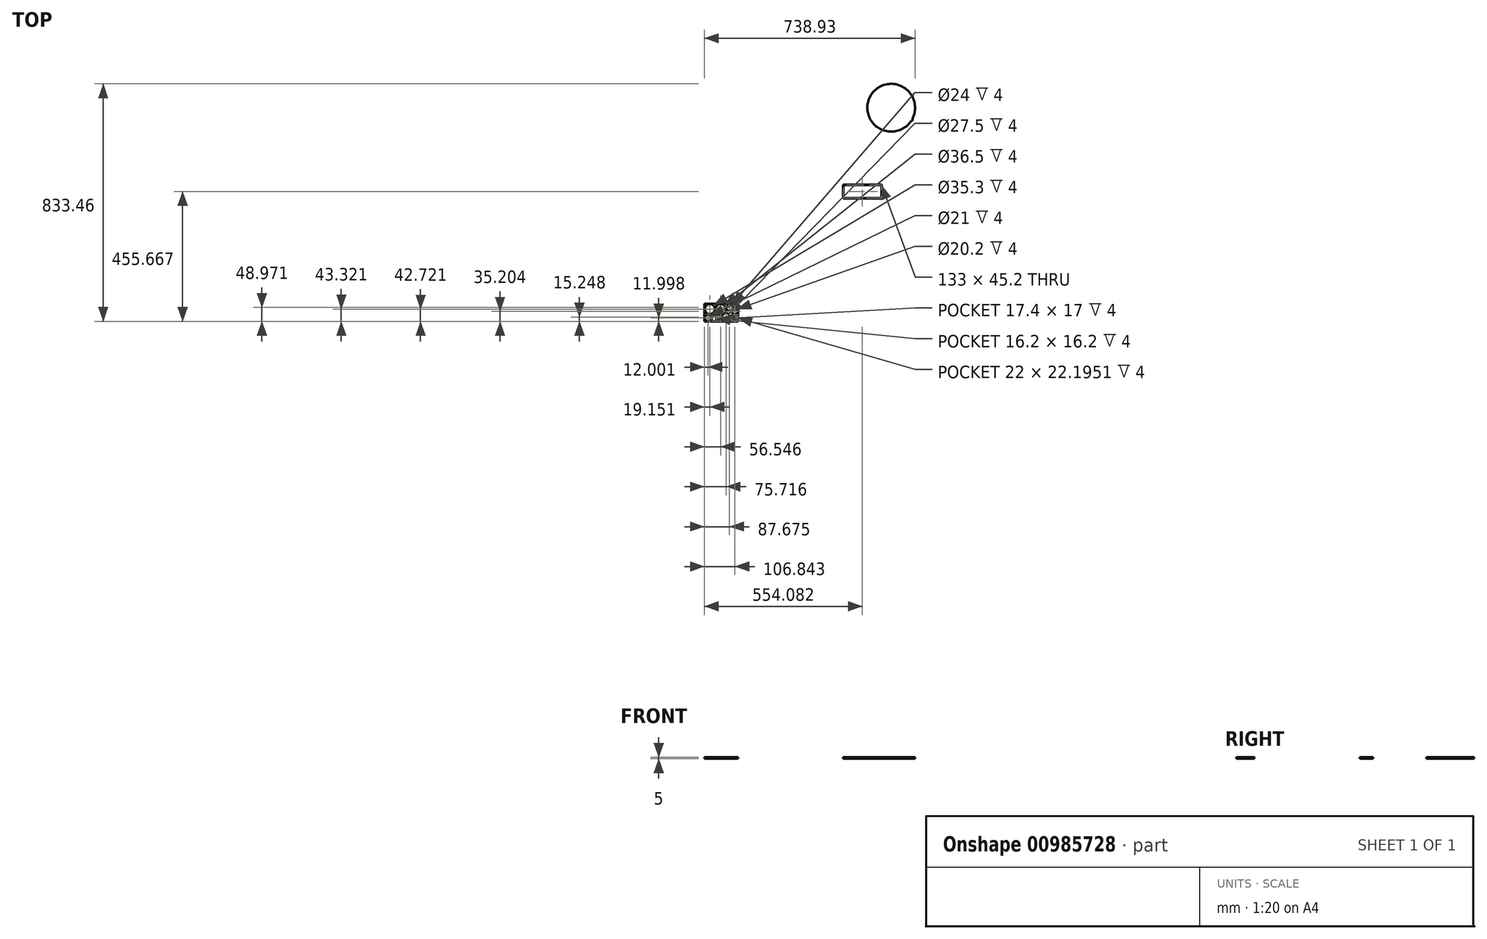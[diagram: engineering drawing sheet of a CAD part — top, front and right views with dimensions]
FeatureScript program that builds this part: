
annotation { "Feature Type Name" : "Feature", "Feature Type Description" : "" }
export const myFeature = defineFeature(function(context is Context, id is Id, definition is map)
    precondition{}
    {
        {
            var Q0;
            Q0=qCreatedBy(makeId("Top.planeOp"),FACE);
            var sketch = newSketch(context, id + "F0", { "sketchPlane" : qUnion([Q0])});
            skCircle(sketch, "E0", {"center": v(-761.21, 497.2) * mm, "radius": 83.82 * mm});
            skLineSegment(sketch, "E1.bottom", {"start": v(-832.69, 451.54) * mm, "end": v(-686.64, 451.54) * mm});
            skLineSegment(sketch, "E1.top", {"start": v(-832.69, 540.44) * mm, "end": v(-686.64, 540.44) * mm});
            skLineSegment(sketch, "E1.left", {"start": v(-832.69, 451.54) * mm, "end": v(-832.69, 540.44) * mm});
            skLineSegment(sketch, "E1.right", {"start": v(-686.64, 451.54) * mm, "end": v(-686.64, 540.44) * mm});
            skCircle(sketch, "E2.5.0.0", {"center": v(-1328.65, -203.47) * mm, "radius": 12 * mm});
            skCircle(sketch, "E3", {"center": v(-1340.6, -237.2) * mm, "radius": 13.75 * mm});
            skCircle(sketch, "E4", {"center": v(-1359.77, -209.72) * mm, "radius": 18.25 * mm});
            skCircle(sketch, "E5", {"center": v(-1397.17, -209.12) * mm, "radius": 17.65 * mm});
            skCircle(sketch, "E6", {"center": v(-1404.32, -240.44) * mm, "radius": 10.5 * mm});
            skCircle(sketch, "E7", {"center": v(-1309.48, -217.24) * mm, "radius": 10.1 * mm});
            skLineSegment(sketch, "E8.bottom", {"start": v(-1373.67, -250.94) * mm, "end": v(-1356.27, -250.94) * mm});
            skLineSegment(sketch, "E8.top", {"start": v(-1373.67, -233.94) * mm, "end": v(-1356.27, -233.94) * mm});
            skLineSegment(sketch, "E8.left", {"start": v(-1373.67, -250.94) * mm, "end": v(-1373.67, -233.94) * mm});
            skLineSegment(sketch, "E8.right", {"start": v(-1356.27, -250.94) * mm, "end": v(-1356.27, -233.94) * mm});
            skLineSegment(sketch, "E9.bottom", {"start": v(-1391.37, -250.94) * mm, "end": v(-1375.17, -250.94) * mm});
            skLineSegment(sketch, "E9.top", {"start": v(-1391.37, -234.74) * mm, "end": v(-1375.17, -234.74) * mm});
            skLineSegment(sketch, "E9.left", {"start": v(-1391.37, -250.94) * mm, "end": v(-1391.37, -234.74) * mm});
            skLineSegment(sketch, "E9.right", {"start": v(-1375.17, -250.94) * mm, "end": v(-1375.17, -234.74) * mm});
            skLineSegment(sketch, "E10.0.1.0", {"start": v(-1321.38, -250.94) * mm, "end": v(-1321.38, -228.94) * mm});
            skLineSegment(sketch, "E10.0.1.1", {"start": v(-1321.38, -228.94) * mm, "end": v(-1299.38, -228.75) * mm});
            skLineSegment(sketch, "E10.0.1.2", {"start": v(-1299.38, -250.94) * mm, "end": v(-1299.38, -228.75) * mm});
            skLineSegment(sketch, "E10.0.1.3", {"start": v(-1321.38, -250.94) * mm, "end": v(-1299.38, -250.94) * mm});
            skLineSegment(sketch, "E11.bottom", {"start": v(-1416.32, -252.44) * mm, "end": v(-1297.88, -252.44) * mm});
            skLineSegment(sketch, "E11.top", {"start": v(-1416.32, -189.97) * mm, "end": v(-1297.88, -189.97) * mm});
            skLineSegment(sketch, "E11.left", {"start": v(-1416.32, -252.44) * mm, "end": v(-1416.32, -189.97) * mm});
            skLineSegment(sketch, "E11.right", {"start": v(-1297.88, -252.44) * mm, "end": v(-1297.88, -189.97) * mm});
            skLineSegment(sketch, "E12.bottom", {"start": v(-929.94, 179.43) * mm, "end": v(-794.54, 179.43) * mm});
            skLineSegment(sketch, "E12.top", {"start": v(-929.94, 227.03) * mm, "end": v(-794.54, 227.03) * mm});
            skLineSegment(sketch, "E12.left", {"start": v(-929.94, 179.43) * mm, "end": v(-929.94, 227.03) * mm});
            skLineSegment(sketch, "E12.right", {"start": v(-794.54, 179.43) * mm, "end": v(-794.54, 227.03) * mm});
            skLineSegment(sketch, "E13.bottom", {"start": v(-928.74, 180.63) * mm, "end": v(-906.74, 180.63) * mm});
            skLineSegment(sketch, "E13.top", {"start": v(-928.74, 202.63) * mm, "end": v(-906.74, 202.63) * mm});
            skLineSegment(sketch, "E13.left", {"start": v(-928.74, 180.63) * mm, "end": v(-928.74, 202.63) * mm});
            skLineSegment(sketch, "E13.right", {"start": v(-906.74, 180.63) * mm, "end": v(-906.74, 202.63) * mm});
            skLineSegment(sketch, "E14.0.1.0", {"start": v(-928.74, 225.83) * mm, "end": v(-906.74, 225.83) * mm});
            skLineSegment(sketch, "E14.0.1.1", {"start": v(-928.74, 203.83) * mm, "end": v(-928.74, 225.83) * mm});
            skLineSegment(sketch, "E14.0.1.2", {"start": v(-906.74, 203.83) * mm, "end": v(-906.74, 225.83) * mm});
            skLineSegment(sketch, "E14.0.1.3", {"start": v(-928.74, 203.83) * mm, "end": v(-906.74, 203.83) * mm});
            skLineSegment(sketch, "E14.1.0.0", {"start": v(-906.74, 202.63) * mm, "end": v(-884.74, 202.63) * mm});
            skLineSegment(sketch, "E14.1.0.2", {"start": v(-884.74, 180.63) * mm, "end": v(-884.74, 202.63) * mm});
            skLineSegment(sketch, "E14.1.0.3", {"start": v(-906.74, 180.63) * mm, "end": v(-884.74, 180.63) * mm});
            skLineSegment(sketch, "E14.1.1.0", {"start": v(-906.74, 225.83) * mm, "end": v(-884.74, 225.83) * mm});
            skLineSegment(sketch, "E14.1.1.1", {"start": v(-906.74, 203.83) * mm, "end": v(-906.74, 225.83) * mm});
            skLineSegment(sketch, "E14.1.1.2", {"start": v(-884.74, 203.83) * mm, "end": v(-884.74, 225.83) * mm});
            skLineSegment(sketch, "E14.1.1.3", {"start": v(-906.74, 203.83) * mm, "end": v(-884.74, 203.83) * mm});
            skLineSegment(sketch, "E14.2.0.0", {"start": v(-884.74, 202.63) * mm, "end": v(-862.74, 202.63) * mm});
            skLineSegment(sketch, "E14.2.0.1", {"start": v(-884.74, 180.63) * mm, "end": v(-884.74, 202.63) * mm});
            skLineSegment(sketch, "E14.2.0.2", {"start": v(-862.74, 180.63) * mm, "end": v(-862.74, 202.63) * mm});
            skLineSegment(sketch, "E14.2.0.3", {"start": v(-884.74, 180.63) * mm, "end": v(-862.74, 180.63) * mm});
            skLineSegment(sketch, "E14.2.1.0", {"start": v(-884.74, 225.83) * mm, "end": v(-862.74, 225.83) * mm});
            skLineSegment(sketch, "E14.2.1.1", {"start": v(-884.74, 203.83) * mm, "end": v(-884.74, 225.83) * mm});
            skLineSegment(sketch, "E14.2.1.2", {"start": v(-862.74, 203.83) * mm, "end": v(-862.74, 225.83) * mm});
            skLineSegment(sketch, "E14.2.1.3", {"start": v(-884.74, 203.83) * mm, "end": v(-862.74, 203.83) * mm});
            skLineSegment(sketch, "E14.3.0.0", {"start": v(-862.74, 202.63) * mm, "end": v(-840.74, 202.63) * mm});
            skLineSegment(sketch, "E14.3.0.1", {"start": v(-862.74, 180.63) * mm, "end": v(-862.74, 202.63) * mm});
            skLineSegment(sketch, "E14.3.0.2", {"start": v(-840.74, 180.63) * mm, "end": v(-840.74, 202.63) * mm});
            skLineSegment(sketch, "E14.3.0.3", {"start": v(-862.74, 180.63) * mm, "end": v(-840.74, 180.63) * mm});
            skLineSegment(sketch, "E14.3.1.0", {"start": v(-862.74, 225.83) * mm, "end": v(-840.74, 225.83) * mm});
            skLineSegment(sketch, "E14.3.1.1", {"start": v(-862.74, 203.83) * mm, "end": v(-862.74, 225.83) * mm});
            skLineSegment(sketch, "E14.3.1.2", {"start": v(-840.74, 203.83) * mm, "end": v(-840.74, 225.83) * mm});
            skLineSegment(sketch, "E14.3.1.3", {"start": v(-862.74, 203.83) * mm, "end": v(-840.74, 203.83) * mm});
            skLineSegment(sketch, "E14.4.0.0", {"start": v(-840.74, 202.63) * mm, "end": v(-818.74, 202.63) * mm});
            skLineSegment(sketch, "E14.4.0.1", {"start": v(-840.74, 180.63) * mm, "end": v(-840.74, 202.63) * mm});
            skLineSegment(sketch, "E14.4.0.2", {"start": v(-818.74, 180.63) * mm, "end": v(-818.74, 202.63) * mm});
            skLineSegment(sketch, "E14.4.0.3", {"start": v(-840.74, 180.63) * mm, "end": v(-818.74, 180.63) * mm});
            skLineSegment(sketch, "E14.4.1.0", {"start": v(-840.74, 225.83) * mm, "end": v(-818.74, 225.83) * mm});
            skLineSegment(sketch, "E14.4.1.1", {"start": v(-840.74, 203.83) * mm, "end": v(-840.74, 225.83) * mm});
            skLineSegment(sketch, "E14.4.1.2", {"start": v(-818.74, 203.83) * mm, "end": v(-818.74, 225.83) * mm});
            skLineSegment(sketch, "E14.4.1.3", {"start": v(-840.74, 203.83) * mm, "end": v(-818.74, 203.83) * mm});
            skLineSegment(sketch, "E14.5.0.0", {"start": v(-818.74, 202.63) * mm, "end": v(-796.74, 202.63) * mm});
            skLineSegment(sketch, "E14.5.0.1", {"start": v(-818.74, 180.63) * mm, "end": v(-818.74, 202.63) * mm});
            skLineSegment(sketch, "E14.5.0.2", {"start": v(-796.74, 180.63) * mm, "end": v(-796.74, 202.63) * mm});
            skLineSegment(sketch, "E14.5.0.3", {"start": v(-818.74, 180.63) * mm, "end": v(-796.74, 180.63) * mm});
            skLineSegment(sketch, "E14.5.1.0", {"start": v(-818.74, 225.83) * mm, "end": v(-796.74, 225.83) * mm});
            skLineSegment(sketch, "E14.5.1.1", {"start": v(-818.74, 203.83) * mm, "end": v(-818.74, 225.83) * mm});
            skLineSegment(sketch, "E14.5.1.2", {"start": v(-796.74, 203.83) * mm, "end": v(-796.74, 225.83) * mm});
            skLineSegment(sketch, "E14.5.1.3", {"start": v(-818.74, 203.83) * mm, "end": v(-796.74, 203.83) * mm});
            skLineSegment(sketch, "E14.direction1", {"start": v(-928.74, 202.63) * mm, "end": v(-906.74, 202.63) * mm, "construction": true});
            skLineSegment(sketch, "E14.direction2", {"start": v(-928.74, 202.63) * mm, "end": v(-928.74, 225.83) * mm, "construction": true});
            skLineSegment(sketch, "E15.0", {"start": v(-928.74, 225.83) * mm, "end": v(-795.74, 225.83) * mm});
            skLineSegment(sketch, "E15.1", {"start": v(-928.74, 180.63) * mm, "end": v(-928.74, 225.83) * mm});
            skLineSegment(sketch, "E15.2", {"start": v(-928.74, 180.63) * mm, "end": v(-795.74, 180.63) * mm});
            skLineSegment(sketch, "E15.3", {"start": v(-795.74, 180.63) * mm, "end": v(-795.74, 225.83) * mm});
            skSolve(sketch);
        }
        {
            var Q0;
            Q0 = qSketchRegion(id + "F0", true);
            extrude(context, id + "F1", {"entities" : qUnion([Q0]), "depth" : 4 * mm, "offsetDistance" : 25 * mm});
        }
        {
            var Q0;
            Q0 = qSketchRegion(id + "F0", true);
            var Q1;
            Q1=makeQuery(id+"F0.imprint","IMPRINT",FACE,{"disambiguationData":[TD([[makeQuery(id+"F0.imprint","IMPRINT",EDGE,{"derivedFrom":sQuery(id+"F0.wireOp",EDGE,"E5")}),1.0]])]});
            var Q2;
            Q2=makeQuery(id+"F0.imprint","IMPRINT",FACE,{"disambiguationData":[TD([[makeQuery(id+"F0.imprint","IMPRINT",EDGE,{"derivedFrom":sQuery(id+"F0.wireOp",EDGE,"E4")}),1.0]])]});
            var Q3;
            Q3=makeQuery(id+"F0.imprint","IMPRINT",FACE,{"disambiguationData":[TD([[makeQuery(id+"F0.imprint","IMPRINT",EDGE,{"derivedFrom":sQuery(id+"F0.wireOp",EDGE,"E2.5.0.0")}),1.0]])]});
            var Q4;
            Q4=makeQuery(id+"F0.imprint","IMPRINT",FACE,{"disambiguationData":[TD([[makeQuery(id+"F0.imprint","IMPRINT",EDGE,{"derivedFrom":sQuery(id+"F0.wireOp",EDGE,"E7")}),1.0]])]});
            var Q5;
            Q5=makeQuery(id+"F0.imprint","IMPRINT",FACE,{"disambiguationData":[TD([[makeQuery(id+"F0.imprint","IMPRINT",EDGE,{"derivedFrom":sQuery(id+"F0.wireOp",EDGE,"E10.0.1.0")}),-1.0]])]});
            var Q6;
            Q6=makeQuery(id+"F0.imprint","IMPRINT",FACE,{"disambiguationData":[TD([[makeQuery(id+"F0.imprint","IMPRINT",EDGE,{"derivedFrom":sQuery(id+"F0.wireOp",EDGE,"E3")}),1.0]])]});
            var Q7;
            Q7=makeQuery(id+"F0.imprint","IMPRINT",FACE,{"disambiguationData":[TD([[makeQuery(id+"F0.imprint","IMPRINT",EDGE,{"derivedFrom":sQuery(id+"F0.wireOp",EDGE,"E8.bottom")}),1.0]])]});
            var Q8;
            Q8=makeQuery(id+"F0.imprint","IMPRINT",FACE,{"disambiguationData":[TD([[makeQuery(id+"F0.imprint","IMPRINT",EDGE,{"derivedFrom":sQuery(id+"F0.wireOp",EDGE,"E9.bottom")}),1.0]])]});
            var Q9;
            Q9=makeQuery(id+"F0.imprint","IMPRINT",FACE,{"disambiguationData":[TD([[makeQuery(id+"F0.imprint","IMPRINT",EDGE,{"derivedFrom":sQuery(id+"F0.wireOp",EDGE,"E6")}),1.0]])]});
            extrude(context, id + "F2", {"entities" : qUnion([Q0, Q1, Q2, Q3, Q4, Q5, Q6, Q7, Q8, Q9]), "operationType" : NewBodyOperationType.ADD, "oppositeDirection" : true, "depth" : 1 * mm, "offsetDistance" : 25 * mm});
        }
    });
